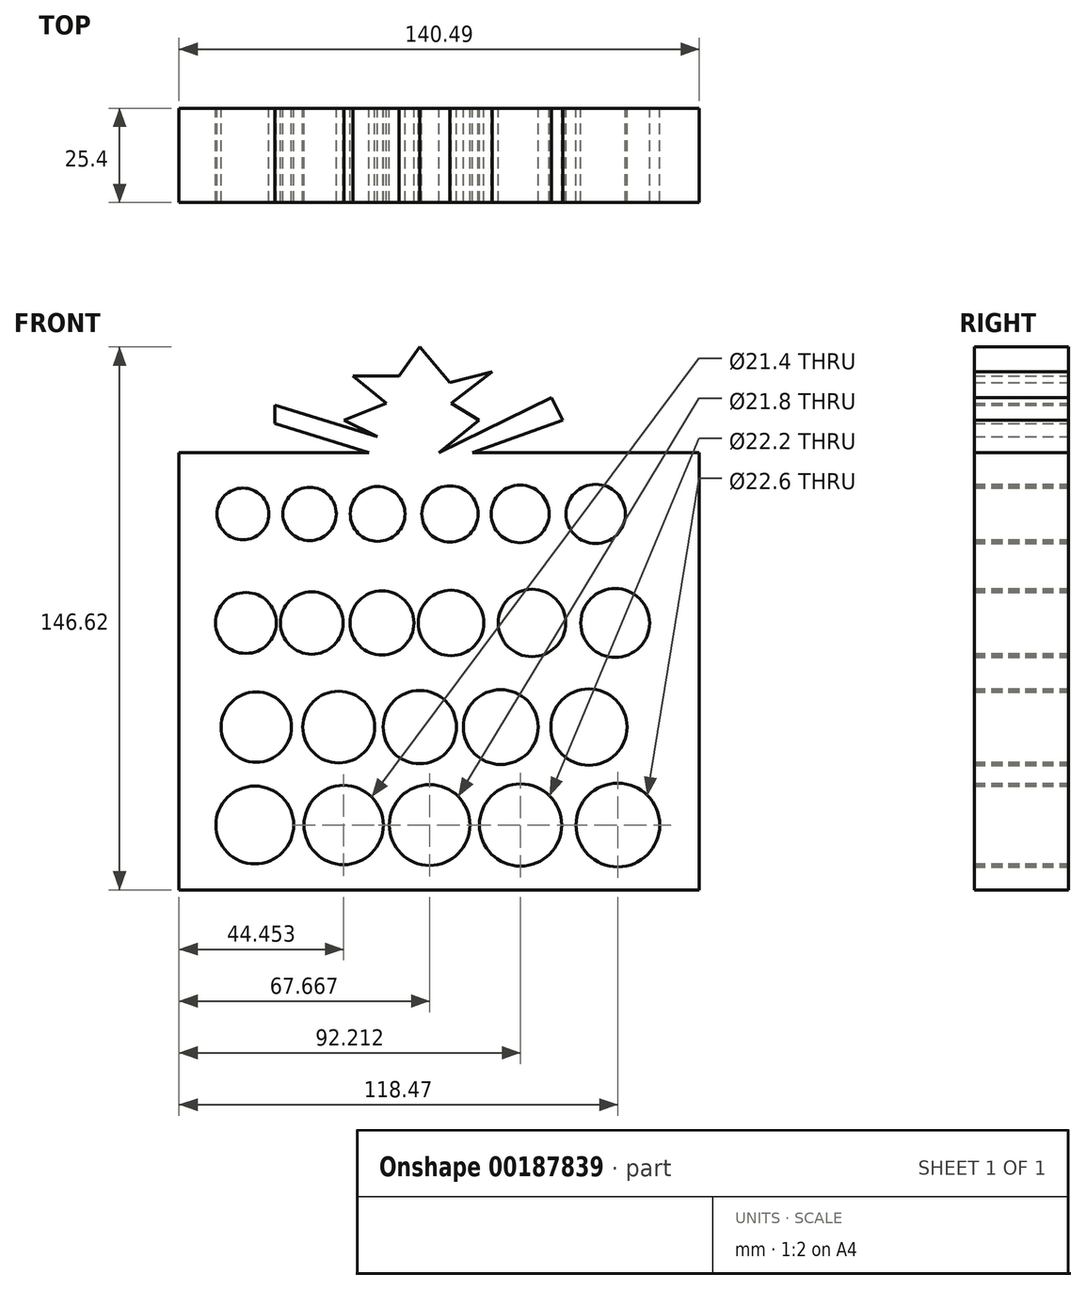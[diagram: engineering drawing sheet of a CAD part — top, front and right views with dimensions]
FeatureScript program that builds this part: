
annotation { "Feature Type Name" : "Feature", "Feature Type Description" : "" }
export const myFeature = defineFeature(function(context is Context, id is Id, definition is map)
    precondition{}
    {
        {
            var Q0;
            Q0=qCreatedBy(makeId("Front.planeOp"),FACE);
            var sketch = newSketch(context, id + "F0", { "sketchPlane" : qUnion([Q0])});
            skCircle(sketch, "E0", {"center": v(-52.68, 30.25) * mm, "radius": 7 * mm});
            skCircle(sketch, "E1", {"center": v(-34.69, 30.25) * mm, "radius": 7.2 * mm});
            skCircle(sketch, "E2", {"center": v(-16.32, 30.25) * mm, "radius": 7.4 * mm});
            skCircle(sketch, "E3", {"center": v(3.2, 30.25) * mm, "radius": 7.6 * mm});
            skCircle(sketch, "E4", {"center": v(22.15, 30.25) * mm, "radius": 7.8 * mm});
            skCircle(sketch, "E5", {"center": v(42.56, 30.25) * mm, "radius": 8 * mm});
            skCircle(sketch, "E6", {"center": v(-51.88, 0.81) * mm, "radius": 8.22 * mm});
            skCircle(sketch, "E7", {"center": v(-34.1, 0.81) * mm, "radius": 8.45 * mm});
            skCircle(sketch, "E8", {"center": v(-15.16, 0.81) * mm, "radius": 8.65 * mm});
            skCircle(sketch, "E9", {"center": v(3.5, 0.81) * mm, "radius": 8.85 * mm});
            skCircle(sketch, "E10", {"center": v(25.36, 0.81) * mm, "radius": 9.1 * mm});
            skCircle(sketch, "E11", {"center": v(47.8, 0.81) * mm, "radius": 9.3 * mm});
            skCircle(sketch, "E12", {"center": v(-49.1, -27.3) * mm, "radius": 9.5 * mm});
            skCircle(sketch, "E13", {"center": v(-26.83, -27.3) * mm, "radius": 9.7 * mm});
            skCircle(sketch, "E14", {"center": v(16.93, -27.3) * mm, "radius": 10.1 * mm});
            skCircle(sketch, "E15", {"center": v(40.72, -27.3) * mm, "radius": 10.3 * mm});
            skCircle(sketch, "E16", {"center": v(-4.95, -27.3) * mm, "radius": 9.9 * mm});
            skCircle(sketch, "E17", {"center": v(-49.47, -53.75) * mm, "radius": 10.5 * mm});
            skCircle(sketch, "E18", {"center": v(-25.5, -53.75) * mm, "radius": 10.7 * mm});
            skCircle(sketch, "E19", {"center": v(-2.28, -53.75) * mm, "radius": 10.9 * mm});
            skCircle(sketch, "E20", {"center": v(22.26, -53.75) * mm, "radius": 11.1 * mm});
            skCircle(sketch, "E21", {"center": v(48.52, -53.75) * mm, "radius": 11.3 * mm});
            skLineSegment(sketch, "E22.bottom", {"start": v(-69.95, 46.78) * mm, "end": v(-18.65, 46.78) * mm});
            skLineSegment(sketch, "E22.top", {"start": v(-69.95, -71.27) * mm, "end": v(70.54, -71.27) * mm});
            skLineSegment(sketch, "E22.left", {"start": v(-69.95, 46.78) * mm, "end": v(-69.95, -71.27) * mm});
            skLineSegment(sketch, "E22.right", {"start": v(70.54, 46.78) * mm, "end": v(70.54, -71.27) * mm});
            skLineSegment(sketch, "E23", {"start": v(-16.32, 51.15) * mm, "end": v(-25.36, 55.53) * mm});
            skLineSegment(sketch, "E24", {"start": v(-25.36, 55.53) * mm, "end": v(-14, 60.19) * mm});
            skLineSegment(sketch, "E25", {"start": v(-14, 60.19) * mm, "end": v(-23.03, 67.48) * mm});
            skLineSegment(sketch, "E26", {"start": v(-23.03, 67.48) * mm, "end": v(-10.5, 67.48) * mm});
            skLineSegment(sketch, "E27", {"start": v(-10.5, 67.48) * mm, "end": v(-4.96, 75.35) * mm});
            skLineSegment(sketch, "E28", {"start": v(-4.96, 75.35) * mm, "end": v(3.2, 65.73) * mm});
            skLineSegment(sketch, "E29", {"start": v(3.2, 65.73) * mm, "end": v(14.57, 68.64) * mm});
            skLineSegment(sketch, "E30", {"start": v(14.57, 68.64) * mm, "end": v(3.5, 60.19) * mm});
            skLineSegment(sketch, "E31", {"start": v(3.5, 60.19) * mm, "end": v(11.08, 55.53) * mm});
            skLineSegment(sketch, "E32", {"start": v(11.08, 55.53) * mm, "end": v(0.3, 46.78) * mm});
            skLineSegment(sketch, "E33", {"start": v(0.3, 46.78) * mm, "end": v(30.6, 61.65) * mm});
            skLineSegment(sketch, "E34", {"start": v(30.6, 61.65) * mm, "end": v(33.6, 55.53) * mm});
            skLineSegment(sketch, "E35", {"start": v(33.6, 55.53) * mm, "end": v(9.33, 46.78) * mm});
            skLineSegment(sketch, "E36", {"start": v(-16.32, 51.15) * mm, "end": v(-44.01, 59.6) * mm});
            skLineSegment(sketch, "E37", {"start": v(-44.01, 59.6) * mm, "end": v(-44.01, 54.65) * mm});
            skLineSegment(sketch, "E38", {"start": v(-44.01, 54.65) * mm, "end": v(-18.65, 46.78) * mm});
            skLineSegment(sketch, "E39.trimOffspring", {"start": v(9.33, 46.78) * mm, "end": v(70.54, 46.78) * mm});
            skPoint(sketch, "E40.orphan", {"position": v(-7.29, 46.78) * mm});
            skSolve(sketch);
        }
        {
            var Q0;
            Q0 = qSketchRegion(id + "F0", true);
            extrude(context, id + "F1", {"entities" : qUnion([Q0]), "depth" : 25.4 * mm});
        }
    });
